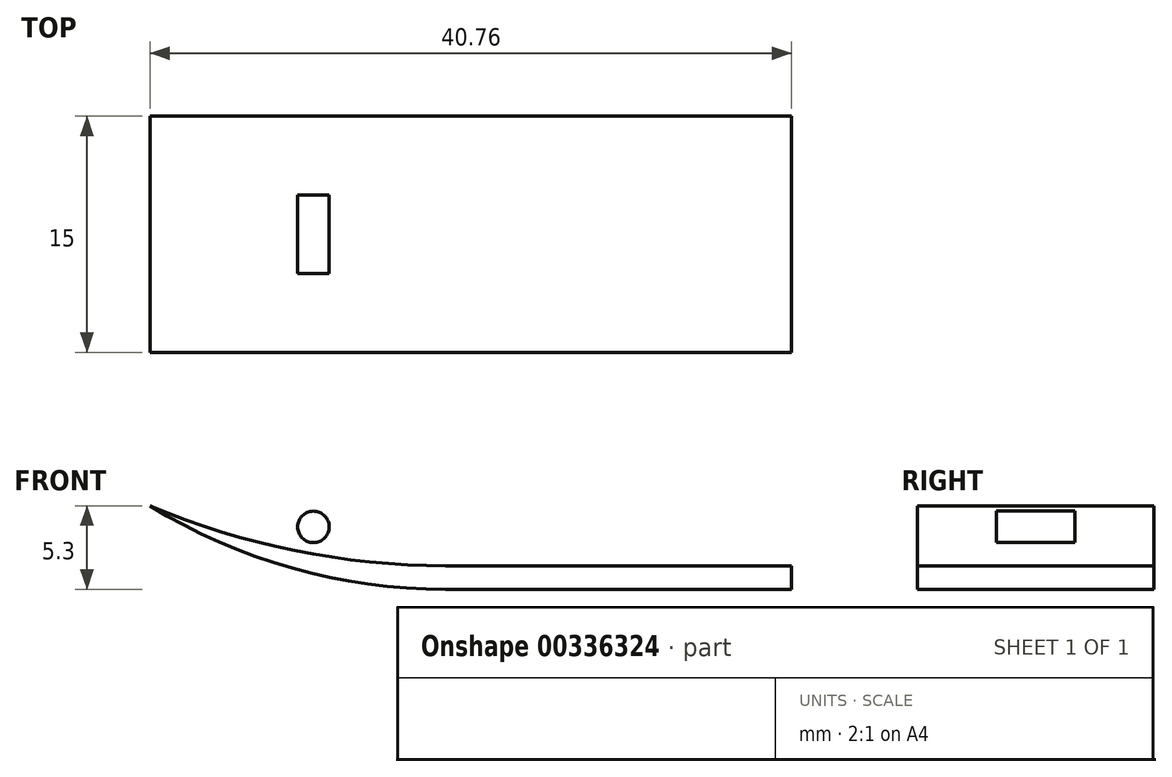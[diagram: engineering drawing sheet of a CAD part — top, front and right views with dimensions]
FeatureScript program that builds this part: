
annotation { "Feature Type Name" : "Feature", "Feature Type Description" : "" }
export const myFeature = defineFeature(function(context is Context, id is Id, definition is map)
    precondition{}
    {
        {
            var Q0;
            Q0=qCreatedBy(makeId("Front.planeOp"),FACE);
            var sketch = newSketch(context, id + "F0", { "sketchPlane" : qUnion([Q0])});
            skLineSegment(sketch, "E0.bottom", {"start": v(0, 0) * mm, "end": v(60, 0) * mm});
            skLineSegment(sketch, "E0.top", {"start": v(0, 1.5) * mm, "end": v(60, 1.5) * mm});
            skLineSegment(sketch, "E0.left", {"start": v(0, 0) * mm, "end": v(0, 1.5) * mm});
            skLineSegment(sketch, "E0.right", {"start": v(60, 0) * mm, "end": v(60, 1.5) * mm});
            skArc(sketch, "E1", {"start": v(-18.76, 5.3) * mm, "mid": v(-9.75, 1.35) * mm, "end": v(0, 0) * mm});
            skArc(sketch, "E2", {"start": v(-18.76, 5.3) * mm, "mid": v(-9.57, 2.46) * mm, "end": v(0, 1.5) * mm});
            skSolve(sketch);
        }
        {
            var Q0;
            Q0=makeQuery(id+"F0.imprint","IMPRINT",FACE,{"disambiguationData":[TD([[makeQuery(id+"F0.imprint","IMPRINT",EDGE,{"derivedFrom":sQuery(id+"F0.wireOp",EDGE,"E0.left")}),1.0]])]});
            var Q1;
            Q1=makeQuery(id+"F0.imprint","IMPRINT",FACE,{"disambiguationData":[TD([[makeQuery(id+"F0.imprint","IMPRINT",EDGE,{"derivedFrom":sQuery(id+"F0.wireOp",EDGE,"E0.bottom")}),1.0]])]});
            extrude(context, id + "F1", {"entities" : qUnion([Q0, Q1]), "depth" : 15 * mm});
        }
        {
            var Q0;
            Q0=makeQuery(id+"F1.opExtrude","SWEPT_FACE",FACE,{"disambiguationData":[OSD([sQuery(id+"F0.wireOp",EDGE,"E0.top")])]});
            var sketch = newSketch(context, id + "F2", { "sketchPlane" : qUnion([Q0])});
            skLineSegment(sketch, "E3.bottom", {"start": v(60, -7.5) * mm, "end": v(0, -7.5) * mm});
            skLineSegment(sketch, "E3.top", {"start": v(60, -5) * mm, "end": v(0, -5) * mm});
            skLineSegment(sketch, "E3.left", {"start": v(60, -7.5) * mm, "end": v(60, -5) * mm});
            skLineSegment(sketch, "E3.right", {"start": v(0, -7.5) * mm, "end": v(0, -5) * mm});
            skLineSegment(sketch, "E4.MirrorCS", {"start": v(60, -10) * mm, "end": v(0, -10) * mm});
            skSolve(sketch);
        }
        {
            var Q0;
            Q0=makeQuery(id+"F2.imprint","IMPRINT",FACE,{"disambiguationData":[TD([[makeQuery(id+"F2.imprint","IMPRINT",EDGE,{"derivedFrom":sQuery(id+"F2.wireOp",EDGE,"E3.bottom")}),-1.0]])]});
            var Q1;
            {var subQ0=sQuery(id+"F2.wireOp",EDGE,"E3.bottom");Q1=makeQuery(id+"F2.imprint","IMPRINT",FACE,{"disambiguationData":[TD([[makeQuery(id+"F2.imprint","IMPRINT",EDGE,{"derivedFrom":subQ0}),1.0]])]});}
            extrude(context, id + "F3", {"entities" : qUnion([Q0, Q1]), "operationType" : NewBodyOperationType.ADD, "depth" : 7 * mm});
        }
        {
            var Q0;
            Q0=makeQuery(id+"F3.opExtrude","SWEPT_FACE",FACE,{"disambiguationData":[OSD([sQuery(id+"F0.wireOp",EDGE,"E0.top"),sQuery(id+"F0.wireOp",EDGE,"E0.left"),sQuery(id+"F0.wireOp",EDGE,"E2"),sQuery(id+"F2.wireOp",EDGE,"E3.right")])]});
            extrude(context, id + "F4", {"entities" : qUnion([Q0]), "operationType" : NewBodyOperationType.ADD, "depth" : 25 * mm});
        }
        {
            var Q0;
            {var subQ0=sQuery(id+"F2.wireOp",EDGE,"E4.MirrorCS");Q0=makeQuery(id+"F4.boolean.opBoolean","MERGE",FACE,{"derivedFrom":[makeQuery(id+"F3.opExtrude","SWEPT_FACE",FACE,{"disambiguationData":[OSD([subQ0])]}),makeQuery(id+"F4.opExtrude","SWEPT_FACE",FACE,{"disambiguationData":[OSD([sQuery(id+"F0.wireOp",EDGE,"E0.top"),sQuery(id+"F0.wireOp",EDGE,"E0.left"),sQuery(id+"F0.wireOp",EDGE,"E2"),subQ0])]})]});}
            var sketch = newSketch(context, id + "F5", { "sketchPlane" : qUnion([Q0])});
            skLineSegment(sketch, "E5", {"start": v(-18.76, 5.3) * mm, "end": v(8.58, 8.5) * mm});
            skCircle(sketch, "E6", {"center": v(23, 5.25) * mm, "radius": 0.75 * mm});
            skSolve(sketch);
        }
        {
            var Q0;
            {var subQ5=sQuery(id+"F5.wireOp",EDGE,"E5");Q0=makeQuery(id+"F5.imprint","IMPRINT",FACE,{"disambiguationData":[TD([[makeQuery(id+"F5.imprint","IMPRINT",EDGE,{"derivedFrom":subQ5}),1.0]])]});}
            var Q1;
            Q1=makeQuery(id+"F5.imprint","IMPRINT",FACE,{"disambiguationData":[TD([[makeQuery(id+"F5.imprint","IMPRINT",EDGE,{"derivedFrom":sQuery(id+"F5.wireOp",EDGE,"E6")}),1.0]])]});
            extrude(context, id + "F6", {"entities" : qUnion([Q0, Q1]), "operationType" : NewBodyOperationType.REMOVE, "endBound" : BoundingType.THROUGH_ALL, "oppositeDirection" : true, "depth" : 25 * mm});
        }
        {
            var Q0;
            {var subQ0=sQuery(id+"F0.wireOp",EDGE,"E0.right");Q0=makeQuery(id+"F3.boolean.opBoolean","MERGE",FACE,{"derivedFrom":[makeQuery(id+"F1.opExtrude","SWEPT_FACE",FACE,{"disambiguationData":[OSD([subQ0])]}),makeQuery(id+"F3.opExtrude","SWEPT_FACE",FACE,{"disambiguationData":[OSD([sQuery(id+"F0.wireOp",EDGE,"E0.top"),subQ0,sQuery(id+"F2.wireOp",EDGE,"E3.left")])]})]});}
            extrude(context, id + "F7", {"entities" : qUnion([Q0]), "operationType" : NewBodyOperationType.ADD, "depth" : 12 * mm});
        }
        {
            var Q0;
            Q0=makeQuery(id+"F7.opExtrude","CAP_FACE",FACE,{"disambiguationData":[OSD([sQuery(id+"F0.wireOp",EDGE,"E0.top"),sQuery(id+"F0.wireOp",EDGE,"E0.right"),sQuery(id+"F2.wireOp",EDGE,"E3.left")])],"isStart":false});
            extrude(context, id + "F8", {"entities" : qUnion([Q0]), "operationType" : NewBodyOperationType.REMOVE, "oppositeDirection" : true, "depth" : 50 * mm});
        }
        {
            var Q0;
            {var subQ0=sQuery(id+"F2.wireOp",EDGE,"E4.MirrorCS");var subQ1=sQuery(id+"F0.wireOp",EDGE,"E0.top");Q0=makeQuery(id+"F7.boolean.opBoolean","MERGE",FACE,{"derivedFrom":[makeQuery(id+"F4.boolean.opBoolean","MERGE",FACE,{"derivedFrom":[makeQuery(id+"F3.opExtrude","SWEPT_FACE",FACE,{"disambiguationData":[OSD([subQ0])]}),makeQuery(id+"F4.opExtrude","SWEPT_FACE",FACE,{"disambiguationData":[OSD([subQ1,sQuery(id+"F0.wireOp",EDGE,"E0.left"),sQuery(id+"F0.wireOp",EDGE,"E2"),subQ0])]})]}),makeQuery(id+"F7.opExtrude","SWEPT_FACE",FACE,{"disambiguationData":[OSD([subQ1,sQuery(id+"F0.wireOp",EDGE,"E0.right"),subQ0])]})]});}
            var sketch = newSketch(context, id + "F9", { "sketchPlane" : qUnion([Q0])});
            skLineSegment(sketch, "E7", {"start": v(8.58, 8.5) * mm, "end": v(-10.57, 8.5) * mm, "construction": true});
            skLineSegment(sketch, "E8", {"start": v(-18.76, 5.3) * mm, "end": v(-18.76, 20.92) * mm, "construction": true});
            skLineSegment(sketch, "E9", {"start": v(-18.76, 20.92) * mm, "end": v(22, 20.92) * mm, "construction": true});
            skLineSegment(sketch, "E10", {"start": v(22, 8.5) * mm, "end": v(22, 20.92) * mm, "construction": true});
            skLineSegment(sketch, "E11", {"start": v(1.62, 20.92) * mm, "end": v(1.62, -6.77) * mm, "construction": true});
            skCircle(sketch, "E12", {"center": v(1.62, 8.5) * mm, "radius": 6.5 * mm, "construction": true});
            skLineSegment(sketch, "E13", {"start": v(-3.62, 3.96) * mm, "end": v(6.85, 3.96) * mm, "construction": true});
            skArc(sketch, "E14", {"start": v(22, 1.5) * mm, "mid": v(16.15, 6.64) * mm, "end": v(8.58, 8.5) * mm});
            skLineSegment(sketch, "E15", {"start": v(1.62, 3.96) * mm, "end": v(11.62, 3.96) * mm, "construction": true});
            skCircle(sketch, "E16", {"center": v(11.62, 3.96) * mm, "radius": 1 * mm});
            skCircle(sketch, "E17.MirrorC", {"center": v(-8.38, 3.96) * mm, "radius": 1 * mm});
            skArc(sketch, "E18", {"start": v(-4.69, 6.95) * mm, "mid": v(2.38, 2.06) * mm, "end": v(8.12, 8.45) * mm});
            skLineSegment(sketch, "E19", {"start": v(-4.69, 6.95) * mm, "end": v(8.12, 8.45) * mm});
            skSolve(sketch);
        }
        {
            var Q0;
            Q0=makeQuery(id+"F9.imprint","IMPRINT",FACE,{"disambiguationData":[TD([[makeQuery(id+"F9.imprint","IMPRINT",EDGE,{"derivedFrom":sQuery(id+"F9.wireOp",EDGE,"E16")}),1.0]])]});
            var Q1;
            Q1=makeQuery(id+"F9.imprint","IMPRINT",FACE,{"disambiguationData":[TD([[makeQuery(id+"F9.imprint","IMPRINT",EDGE,{"derivedFrom":sQuery(id+"F9.wireOp",EDGE,"E17.MirrorC")}),-1.0]])]});
            var Q2;
            Q2=makeQuery(id+"F9.imprint","IMPRINT",FACE,{"disambiguationData":[TD([[makeQuery(id+"F9.imprint","IMPRINT",EDGE,{"derivedFrom":sQuery(id+"F9.wireOp",EDGE,"E14")}),-1.0]])]});
            var Q3;
            Q3=makeQuery(id+"F9.imprint","IMPRINT",FACE,{"disambiguationData":[TD([[makeQuery(id+"F9.imprint","IMPRINT",EDGE,{"derivedFrom":sQuery(id+"F9.wireOp",EDGE,"E18")}),1.0]])]});
            extrude(context, id + "F10", {"entities" : qUnion([Q0, Q1, Q2, Q3]), "operationType" : NewBodyOperationType.REMOVE, "endBound" : BoundingType.THROUGH_ALL, "oppositeDirection" : true, "depth" : 25 * mm});
        }
    });
